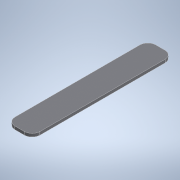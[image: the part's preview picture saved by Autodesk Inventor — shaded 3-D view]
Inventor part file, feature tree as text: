
AUTODESK INVENTOR PART (.ipt)
format: ipt  version: 2022.1 (Build 261234000, 234)  size: 107,008 bytes
history: native  units: mm
features: other x1, extrude x1, sketch x1
ambient origin geometry x8: Origin, YZ Plane, XZ Plane, XY Plane, X Axis, Y Axis, Z Axis, Center Point
bodies: Body1 (feature_tree)
feature tree (3):
  other  "Sólido1"
  extrude  "Extrusión1"  Depth=160.0mm
  sketch  "Boceto1"  dims[d0=900.0mm d1=160.0mm d2=50.0mm d3=50.0mm d4=50.0mm d5=50.0mm d6=20.0mm d7=0.0mm]
